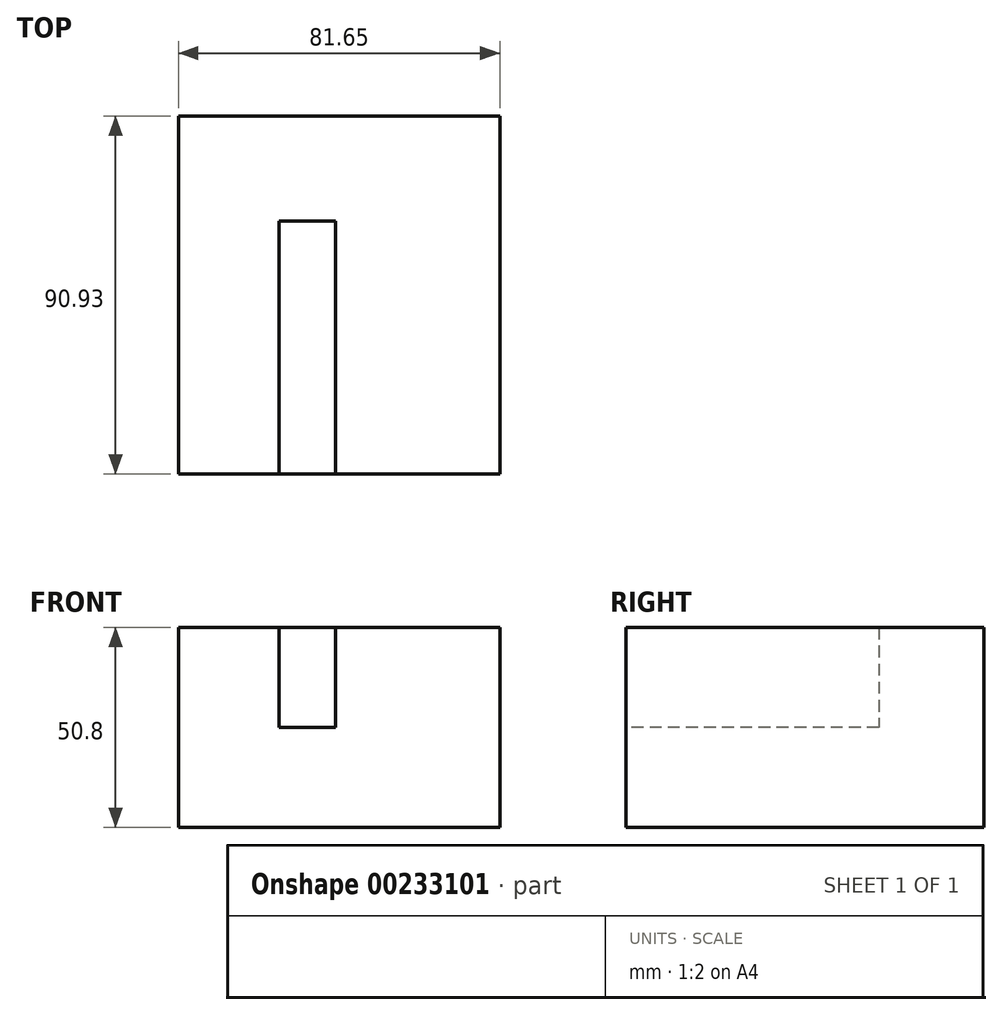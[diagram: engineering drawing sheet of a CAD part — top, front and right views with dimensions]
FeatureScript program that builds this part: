
annotation { "Feature Type Name" : "Feature", "Feature Type Description" : "" }
export const myFeature = defineFeature(function(context is Context, id is Id, definition is map)
    precondition{}
    {
        {
            var Q0;
            Q0=qCreatedBy(makeId("Top.planeOp"),FACE);
            var sketch = newSketch(context, id + "F0", { "sketchPlane" : qUnion([Q0])});
            skLineSegment(sketch, "E0.bottom", {"start": v(-10.18, -45.64) * mm, "end": v(-91.83, -45.64) * mm});
            skLineSegment(sketch, "E0.top", {"start": v(-10.18, 45.3) * mm, "end": v(-91.83, 45.3) * mm});
            skLineSegment(sketch, "E0.left", {"start": v(-10.18, -45.64) * mm, "end": v(-10.18, 45.3) * mm});
            skLineSegment(sketch, "E0.right", {"start": v(-91.83, -45.64) * mm, "end": v(-91.83, 45.3) * mm});
            skSolve(sketch);
        }
        {
            var Q0;
            Q0 = qSketchRegion(id + "F0", true);
            extrude(context, id + "F1", {"entities" : qUnion([Q0]), "depth" : 25.4 * mm});
        }
        {
            var Q0;
            Q0=makeQuery(id+"F1.opExtrude","CAP_FACE",FACE,{"disambiguationData":[OSD([sQuery(id+"F0.wireOp",EDGE,"E0.bottom"),sQuery(id+"F0.wireOp",EDGE,"E0.top"),sQuery(id+"F0.wireOp",EDGE,"E0.left"),sQuery(id+"F0.wireOp",EDGE,"E0.right")])],"isStart":false});
            var sketch = newSketch(context, id + "F2", { "sketchPlane" : qUnion([Q0])});
            skLineSegment(sketch, "E1.bottom", {"start": v(-66.3, 18.64) * mm, "end": v(-51.87, 18.64) * mm});
            skLineSegment(sketch, "E1.top", {"start": v(-66.3, -67.23) * mm, "end": v(-51.87, -67.23) * mm});
            skLineSegment(sketch, "E1.left", {"start": v(-66.3, 18.64) * mm, "end": v(-66.3, -67.23) * mm});
            skLineSegment(sketch, "E1.right", {"start": v(-51.87, 18.64) * mm, "end": v(-51.87, -67.23) * mm});
            skSolve(sketch);
        }
        {
            var Q0;
            {var subQ1=sQuery(id+"F2.wireOp",EDGE,"E1.bottom");Q0=makeQuery(id+"F2.imprint","IMPRINT",FACE,{"disambiguationData":[TD([[makeQuery(id+"F2.imprint","IMPRINT",EDGE,{"derivedFrom":subQ1}),1.0]])]});}
            extrude(context, id + "F3", {"entities" : qUnion([Q0]), "operationType" : NewBodyOperationType.ADD, "depth" : 25.4 * mm});
        }
    });
